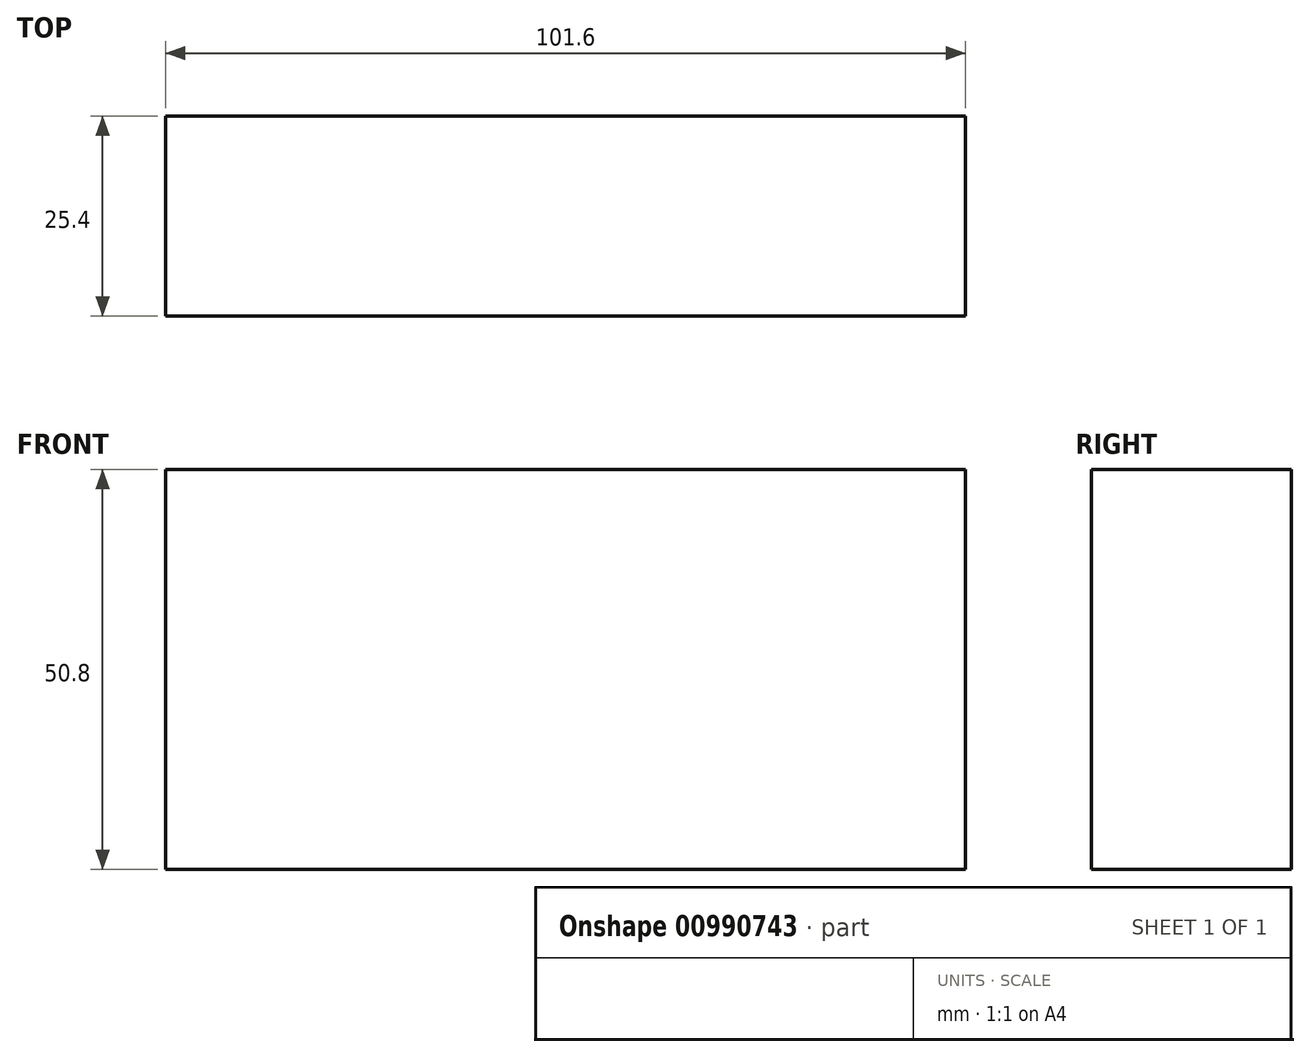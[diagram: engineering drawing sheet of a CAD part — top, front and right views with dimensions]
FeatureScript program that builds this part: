
annotation { "Feature Type Name" : "Feature", "Feature Type Description" : "" }
export const myFeature = defineFeature(function(context is Context, id is Id, definition is map)
    precondition{}
    {
        {
            var Q0;
            Q0=qCreatedBy(makeId("Front.planeOp"),FACE);
            var sketch = newSketch(context, id + "F0", { "sketchPlane" : qUnion([Q0])});
            skLineSegment(sketch, "E0.bottom", {"start": v(25.4, 25.4) * mm, "end": v(-25.4, 25.4) * mm});
            skLineSegment(sketch, "E0.top", {"start": v(25.4, -25.4) * mm, "end": v(-25.4, -25.4) * mm});
            skLineSegment(sketch, "E0.left", {"start": v(25.4, 25.4) * mm, "end": v(25.4, -25.4) * mm});
            skLineSegment(sketch, "E0.right", {"start": v(-25.4, 25.4) * mm, "end": v(-25.4, -25.4) * mm});
            skPoint(sketch, "E0.middle", {"position": v(0, 0) * mm});
            skSolve(sketch);
        }
        {
            var Q0;
            Q0=makeQuery(id+"F0.imprint","IMPRINT",FACE,{"disambiguationData":[TD([[makeQuery(id+"F0.imprint","IMPRINT",EDGE,{"derivedFrom":sQuery(id+"F0.wireOp",EDGE,"E0.bottom")}),1.0]])]});
            extrude(context, id + "F1", {"entities" : qUnion([Q0]), "endBound" : BoundingType.SYMMETRIC, "depth" : 25.4 * mm, "offsetDistance" : 25.4 * mm});
        }
        {
            var Q0;
            Q0=makeQuery(id+"F1.opExtrude","SWEPT_BODY",BODY,{"disambiguationData":[OSD([sQuery(id+"F0.wireOp",EDGE,"E0.bottom"),sQuery(id+"F0.wireOp",EDGE,"E0.top"),sQuery(id+"F0.wireOp",EDGE,"E0.left"),sQuery(id+"F0.wireOp",EDGE,"E0.right")])]});
            var Q1;
            Q1=makeQuery(id+"F1.opExtrude","SWEPT_FACE",FACE,{"disambiguationData":[OSD([sQuery(id+"F0.wireOp",EDGE,"E0.right")])]});
            mirror(context, id + "F2", {"operationType" : NewBodyOperationType.ADD, "entities" : qUnion([Q0]), "mirrorPlane" : qUnion([Q1])});
        }
    });
